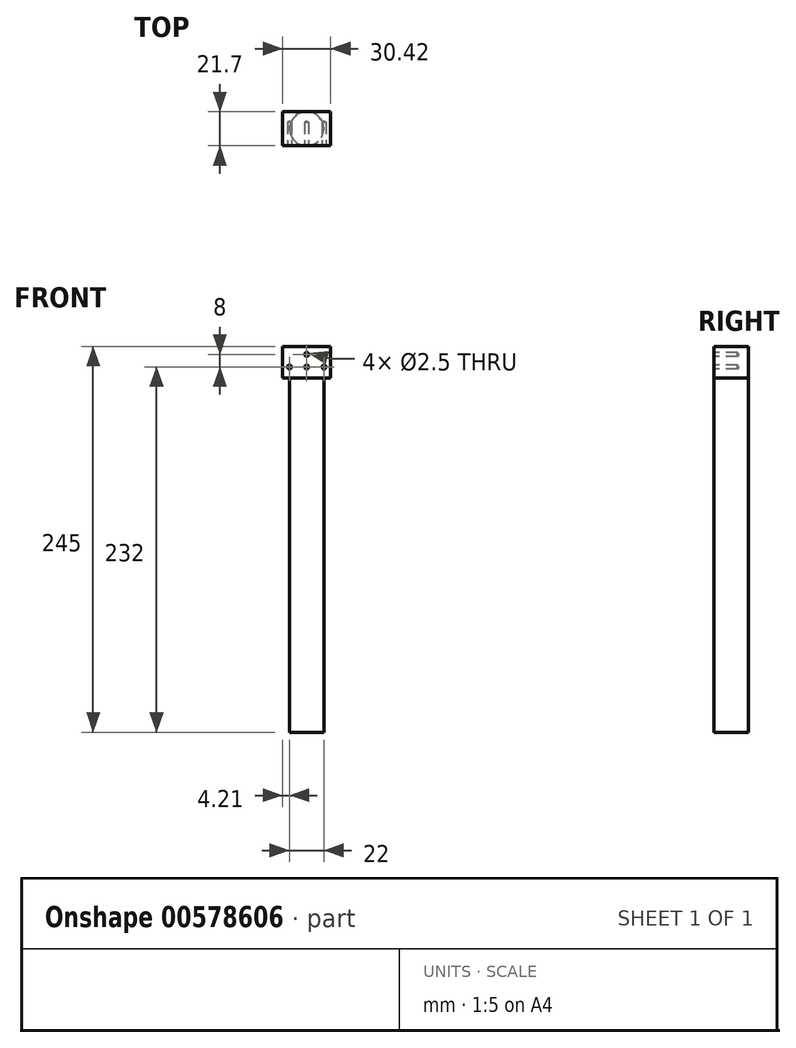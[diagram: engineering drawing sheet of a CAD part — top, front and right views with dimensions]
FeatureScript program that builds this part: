
annotation { "Feature Type Name" : "Feature", "Feature Type Description" : "" }
export const myFeature = defineFeature(function(context is Context, id is Id, definition is map)
    precondition{}
    {
        {
            var Q0;
            Q0=qCreatedBy(makeId("Top.planeOp"),FACE);
            var sketch = newSketch(context, id + "F0", { "sketchPlane" : qUnion([Q0])});
            skCircle(sketch, "E0", {"center": v(0, 0) * mm, "radius": 10.85 * mm});
            skSolve(sketch);
        }
        {
            var Q0;
            Q0=makeQuery(id+"F0.imprint","IMPRINT",FACE,{"disambiguationData":[TD([[makeQuery(id+"F0.imprint","IMPRINT",EDGE,{"derivedFrom":sQuery(id+"F0.wireOp",EDGE,"E0")}),1.0]])]});
            extrude(context, id + "F1", {"entities" : qUnion([Q0]), "depth" : 225 * mm, "offsetDistance" : 25 * mm});
        }
        {
            var Q0;
            Q0=makeQuery(id+"F1.opExtrude","CAP_EDGE",EDGE,{"disambiguationData":[OSD([sQuery(id+"F0.wireOp",EDGE,"E0")])],"isStart":false});
            cPlane(context, id + "F2", {"entities" : qUnion([Q0]), "cplaneType" : CPlaneType.LINE_ANGLE, "offset" : 25 * mm, "angle" : 0 * degree, "width" : 150 * mm, "height" : 150 * mm});
        }
        {
            var Q0;
            Q0=qCreatedBy(id+"F2.planeOp",FACE);
            var sketch = newSketch(context, id + "F3", { "sketchPlane" : qUnion([Q0])});
            skLineSegment(sketch, "E1", {"start": v(-10.84, 225) * mm, "end": v(-10.84, 245) * mm});
            skLineSegment(sketch, "E2", {"start": v(-10.84, 245) * mm, "end": v(10.85, 225) * mm});
            skLineSegment(sketch, "E3", {"start": v(10.85, 225) * mm, "end": v(-10.84, 225) * mm});
            skLineSegment(sketch, "E4", {"start": v(-10.84, 245) * mm, "end": v(10.85, 245) * mm});
            skLineSegment(sketch, "E5", {"start": v(10.85, 245) * mm, "end": v(10.85, 225) * mm});
            skSolve(sketch);
        }
        {
            var Q0;
            Q0=makeQuery(id+"F3.imprint","IMPRINT",FACE,{"disambiguationData":[TD([[makeQuery(id+"F3.imprint","IMPRINT",EDGE,{"derivedFrom":sQuery(id+"F3.wireOp",EDGE,"E1")}),-1.0]])]});
            var Q1;
            Q1=makeQuery(id+"F3.imprint","IMPRINT",FACE,{"disambiguationData":[TD([[makeQuery(id+"F3.imprint","IMPRINT",EDGE,{"derivedFrom":sQuery(id+"F3.wireOp",EDGE,"E2")}),1.0]])]});
            extrude(context, id + "F4", {"entities" : qUnion([Q0, Q1]), "operationType" : NewBodyOperationType.ADD, "endBound" : BoundingType.SYMMETRIC, "depth" : 30.42 * mm, "offsetDistance" : 25 * mm});
        }
        {
            var Q0;
            Q0=makeQuery(id+"F4.opExtrude","SWEPT_FACE",FACE,{"disambiguationData":[OSD([sQuery(id+"F3.wireOp",EDGE,"E1")])]});
            var sketch = newSketch(context, id + "F5", { "sketchPlane" : qUnion([Q0])});
            skPoint(sketch, "E6", {"position": v(11, 232) * mm});
            skPoint(sketch, "E7", {"position": v(0, 232) * mm});
            skPoint(sketch, "E8", {"position": v(-11, 232) * mm});
            skPoint(sketch, "E9", {"position": v(0, 240) * mm});
            skLineSegment(sketch, "E10", {"start": v(-15.21, 240) * mm, "end": v(15.21, 240) * mm, "construction": true});
            skLineSegment(sketch, "E11", {"start": v(15.21, 232) * mm, "end": v(-15.21, 232) * mm, "construction": true});
            skLineSegment(sketch, "E12", {"start": v(0, 240) * mm, "end": v(0, 232) * mm});
            skLineSegment(sketch, "E13", {"start": v(11, 232) * mm, "end": v(0, 240) * mm});
            skLineSegment(sketch, "E14", {"start": v(-11, 232) * mm, "end": v(0, 240) * mm});
            skLineSegment(sketch, "E15", {"start": v(0, 232) * mm, "end": v(-11, 232) * mm});
            skLineSegment(sketch, "E16", {"start": v(0, 232) * mm, "end": v(11, 232) * mm});
            skSolve(sketch);
        }
        {
            var Q0;
            Q0=sQuery(id+"F5.wireOp",VERTEX,"E6");
            var Q1;
            Q1=sQuery(id+"F5.wireOp",VERTEX,"E7");
            var Q2;
            Q2=sQuery(id+"F5.wireOp",VERTEX,"E8");
            var Q3;
            Q3=sQuery(id+"F5.wireOp",VERTEX,"E9");
            var Q4;
            Q4=makeQuery(id+"F1.opExtrude","SWEPT_BODY",BODY,{"disambiguationData":[OSD([sQuery(id+"F0.wireOp",EDGE,"E0")])]});
            hole(context, id + "F6", {"style" : HoleStyle.SIMPLE, "endStyle" : HoleEndStyle.BLIND, "standardTappedOrClearance" : lookupTablePath({ "standard" : "ISO", "engagement" : "75%", "pitch" : "0.5 mm", "size" : "M3", "type" : "Tapped" }), "standardBlindInLast" : lookupTablePath({ "standard" : "ISO", "engagement" : "75%", "pitch" : "0.5 mm", "size" : "M3", "type" : "Tapped" }), "holeDiameter" : 2.5 * mm, "majorDiameter" : 3 * mm, "showTappedDepth" : true, "holeDepth" : 15 * mm, "isTappedThrough" : true, "tappedDepth" : 15 * mm, "tapClearance" : 0, "startFromSketch" : true, "locations" : qUnion([Q0, Q1, Q2, Q3]), "scope" : qUnion([Q4])});
        }
    });
